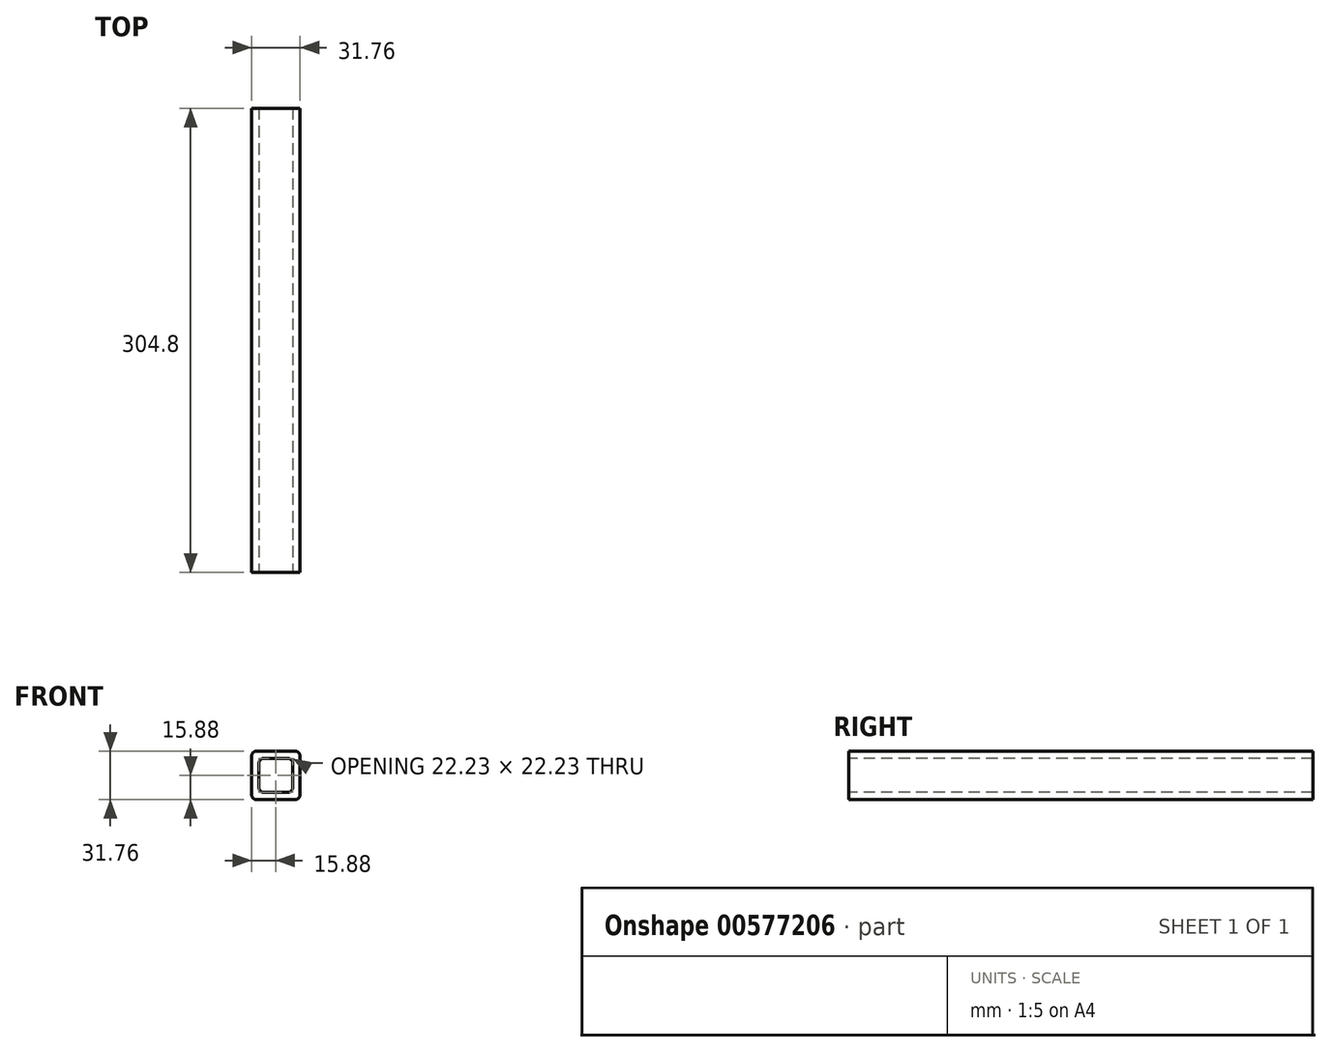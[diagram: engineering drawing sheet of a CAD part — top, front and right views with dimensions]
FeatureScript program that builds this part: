
annotation { "Feature Type Name" : "Feature", "Feature Type Description" : "" }
export const myFeature = defineFeature(function(context is Context, id is Id, definition is map)
    precondition{}
    {
        {
            var Q0;
            Q0=qCreatedBy(makeId("Front.planeOp"),FACE);
            var sketch = newSketch(context, id + "F0", { "sketchPlane" : qUnion([Q0])});
            skLineSegment(sketch, "E0.bottom", {"start": v(12.7, 15.88) * mm, "end": v(-12.7, 15.88) * mm});
            skLineSegment(sketch, "E0.top", {"start": v(12.7, -15.88) * mm, "end": v(-12.7, -15.88) * mm});
            skLineSegment(sketch, "E0.left", {"start": v(15.88, 12.7) * mm, "end": v(15.88, -12.7) * mm});
            skLineSegment(sketch, "E0.right", {"start": v(-15.88, 12.7) * mm, "end": v(-15.88, -12.7) * mm});
            skPoint(sketch, "E0.middle", {"position": v(0, 0) * mm});
            skLineSegment(sketch, "E1.bottom", {"start": v(7.94, 11.11) * mm, "end": v(-7.94, 11.11) * mm});
            skLineSegment(sketch, "E1.top", {"start": v(7.94, -11.11) * mm, "end": v(-7.94, -11.11) * mm});
            skLineSegment(sketch, "E1.left", {"start": v(11.11, 7.94) * mm, "end": v(11.11, -7.94) * mm});
            skLineSegment(sketch, "E1.right", {"start": v(-11.11, 7.94) * mm, "end": v(-11.11, -7.94) * mm});
            skPoint(sketch, "E2.visualSharp", {"position": v(-15.88, 15.88) * mm});
            skArc(sketch, "E2.filletArc", {"start": v(-12.7, 15.88) * mm, "mid": v(-14.95, 14.95) * mm, "end": v(-15.88, 12.7) * mm});
            skPoint(sketch, "E3.visualSharp", {"position": v(15.88, 15.88) * mm});
            skArc(sketch, "E3.filletArc", {"start": v(15.88, 12.7) * mm, "mid": v(14.95, 14.95) * mm, "end": v(12.7, 15.88) * mm});
            skPoint(sketch, "E4.visualSharp", {"position": v(15.88, -15.88) * mm});
            skArc(sketch, "E4.filletArc", {"start": v(12.7, -15.88) * mm, "mid": v(14.95, -14.95) * mm, "end": v(15.88, -12.7) * mm});
            skPoint(sketch, "E5.visualSharp", {"position": v(-15.88, -15.88) * mm});
            skArc(sketch, "E5.filletArc", {"start": v(-15.88, -12.7) * mm, "mid": v(-14.95, -14.95) * mm, "end": v(-12.7, -15.88) * mm});
            skPoint(sketch, "E6.visualSharp", {"position": v(-11.11, -11.11) * mm});
            skArc(sketch, "E6.filletArc", {"start": v(-11.11, -7.94) * mm, "mid": v(-10.18, -10.18) * mm, "end": v(-7.94, -11.11) * mm});
            skPoint(sketch, "E7.visualSharp", {"position": v(-11.11, 11.11) * mm});
            skArc(sketch, "E7.filletArc", {"start": v(-7.94, 11.11) * mm, "mid": v(-10.18, 10.18) * mm, "end": v(-11.11, 7.94) * mm});
            skPoint(sketch, "E8.visualSharp", {"position": v(11.11, 11.11) * mm});
            skArc(sketch, "E8.filletArc", {"start": v(11.11, 7.94) * mm, "mid": v(10.18, 10.18) * mm, "end": v(7.94, 11.11) * mm});
            skPoint(sketch, "E9.visualSharp", {"position": v(11.11, -11.11) * mm});
            skArc(sketch, "E9.filletArc", {"start": v(7.94, -11.11) * mm, "mid": v(10.18, -10.18) * mm, "end": v(11.11, -7.94) * mm});
            skSolve(sketch);
        }
        {
            var Q0;
            Q0 = qSketchRegion(id + "F0", true);
            extrude(context, id + "F1", {"entities" : qUnion([Q0]), "oppositeDirection" : true, "depth" : 304.8 * mm, "offsetDistance" : 25.4 * mm});
        }
    });
